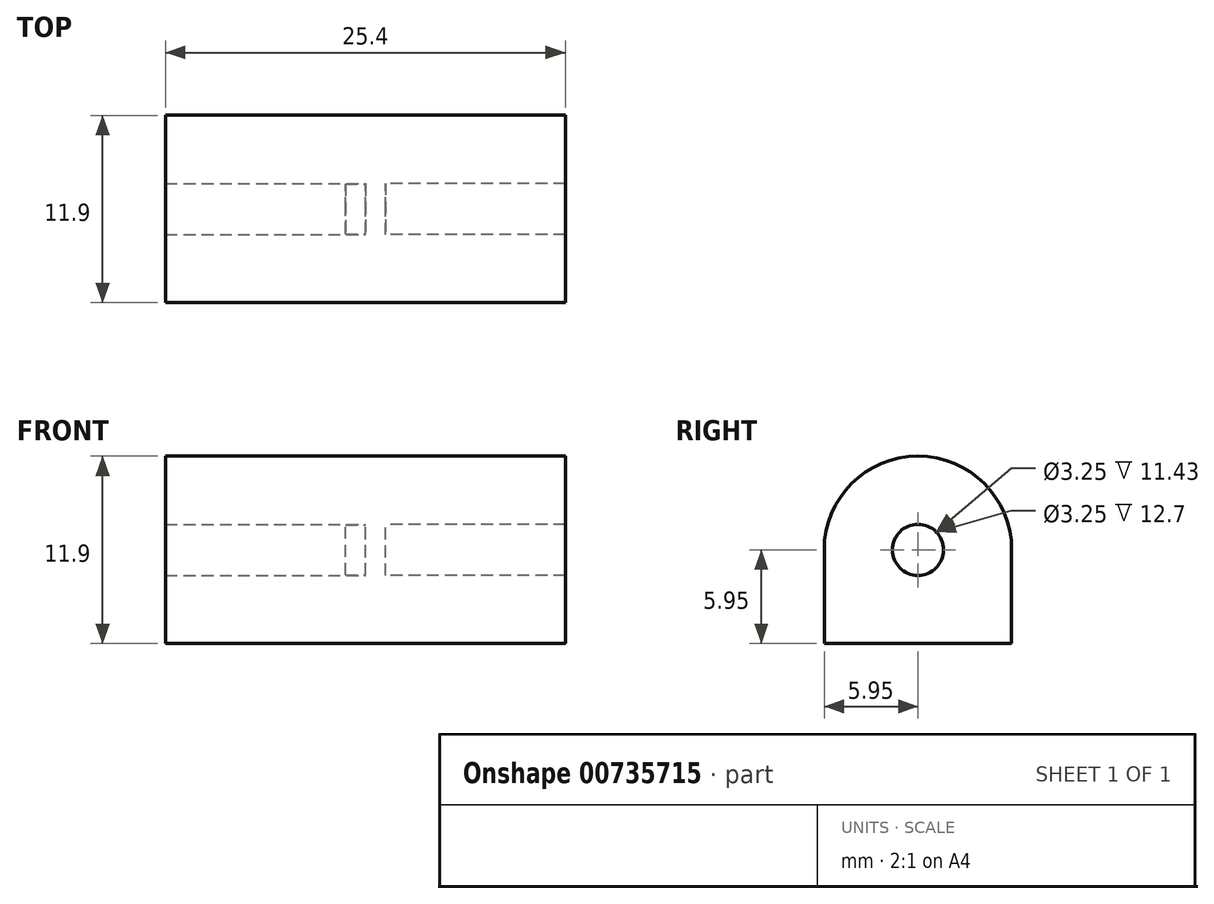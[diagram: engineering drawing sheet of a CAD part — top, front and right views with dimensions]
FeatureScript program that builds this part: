
annotation { "Feature Type Name" : "Feature", "Feature Type Description" : "" }
export const myFeature = defineFeature(function(context is Context, id is Id, definition is map)
    precondition{}
    {
        {
            var Q0;
            Q0=qCreatedBy(makeId("Right.planeOp"),FACE);
            var sketch = newSketch(context, id + "F0", { "sketchPlane" : qUnion([Q0])});
            skPoint(sketch, "E0", {"position": v(0, 0) * mm});
            skCircle(sketch, "E1", {"center": v(0, 0) * mm, "radius": 1.63 * mm});
            skCircle(sketch, "E2", {"center": v(0, 0) * mm, "radius": 5.95 * mm});
            skLineSegment(sketch, "E3", {"start": v(-5.95, 0) * mm, "end": v(-5.95, -5.95) * mm});
            skLineSegment(sketch, "E4", {"start": v(0, -5.95) * mm, "end": v(-5.95, -5.95) * mm});
            skLineSegment(sketch, "E5.MirrorCS", {"start": v(5.95, 0) * mm, "end": v(5.95, -5.95) * mm});
            skLineSegment(sketch, "E6.MirrorCS", {"start": v(0, -5.95) * mm, "end": v(5.95, -5.95) * mm});
            skSolve(sketch);
        }
        {
            var Q0;
            Q0=makeQuery(id+"F0.imprint","IMPRINT",FACE,{"disambiguationData":[TD([[makeQuery(id+"F0.imprint","IMPRINT",EDGE,{"derivedFrom":sQuery(id+"F0.wireOp",EDGE,"E1")}),-1.0]])]});
            var Q1;
            {var subQ0=sQuery(id+"F0.wireOp",EDGE,"LAxV7YV0-o3Pd-S6Uu-0Qhw-ZbayDCktP1mj");Q1=makeQuery(id+"F0.imprint","IMPRINT",FACE,{"disambiguationData":[TD([[makeQuery(id+"F0.imprint","IMPRINT",EDGE,{"derivedFrom":subQ0}),-1.0]])]});}
            var Q2;
            {var subQ0=sQuery(id+"F0.wireOp",EDGE,"a4slryUw-I1Qj-lKQd-dN9I-7wWvJhmVjrbc");Q2=makeQuery(id+"F0.imprint","IMPRINT",FACE,{"disambiguationData":[TD([[makeQuery(id+"F0.imprint","IMPRINT",EDGE,{"derivedFrom":subQ0}),-1.0]])]});}
            var Q3;
            {var subQ0=sQuery(id+"F0.wireOp",EDGE,"bc7faf61-ac77-4107-8db6-a5a29b3dcb3c0.MirrorCS");Q3=makeQuery(id+"F0.imprint","IMPRINT",FACE,{"disambiguationData":[TD([[makeQuery(id+"F0.imprint","IMPRINT",EDGE,{"derivedFrom":subQ0}),1.0]])]});}
            var Q4;
            {var subQ0=sQuery(id+"F0.wireOp",EDGE,"V9x5OHFx-vdUW-RZON-vu1w-wDtBgKBEigPh");Q4=makeQuery(id+"F0.imprint","IMPRINT",FACE,{"disambiguationData":[TD([[makeQuery(id+"F0.imprint","IMPRINT",EDGE,{"derivedFrom":subQ0}),-1.0]])]});}
            var Q5;
            {var subQ2=sQuery(id+"F0.wireOp",EDGE,"E5.MirrorCS");Q5=makeQuery(id+"F0.imprint","IMPRINT",FACE,{"disambiguationData":[TD([[makeQuery(id+"F0.imprint","IMPRINT",EDGE,{"derivedFrom":subQ2}),-1.0]])]});}
            var Q6;
            {var subQ0=sQuery(id+"F0.wireOp",EDGE,"E3");Q6=makeQuery(id+"F0.imprint","IMPRINT",FACE,{"disambiguationData":[TD([[makeQuery(id+"F0.imprint","IMPRINT",EDGE,{"derivedFrom":subQ0}),1.0]])]});}
            extrude(context, id + "F1", {"entities" : qUnion([Q0, Q1, Q2, Q3, Q4, Q5, Q6]), "depth" : 12.7 * mm, "offsetDistance" : 25.4 * mm});
        }
        {
            var Q0;
            Q0=qCreatedBy(makeId("Right.planeOp"),FACE);
            var sketch = newSketch(context, id + "F2", { "sketchPlane" : qUnion([Q0])});
            skCircle(sketch, "E7", {"center": v(0, 0) * mm, "radius": 1.59 * mm});
            skSolve(sketch);
        }
        {
            var Q0;
            Q0=makeQuery(id+"F0.imprint","IMPRINT",FACE,{"disambiguationData":[TD([[makeQuery(id+"F0.imprint","IMPRINT",EDGE,{"derivedFrom":sQuery(id+"F0.wireOp",EDGE,"E1")}),1.0]])]});
            extrude(context, id + "F3", {"entities" : qUnion([Q0]), "depth" : 1.27 * mm, "offsetDistance" : 25.4 * mm});
        }
        {
            var Q0;
            Q0=makeQuery(id+"F2.imprint","IMPRINT",FACE,{"disambiguationData":[TD([[makeQuery(id+"F2.imprint","IMPRINT",EDGE,{"derivedFrom":sQuery(id+"F2.wireOp",EDGE,"E7")}),1.0]])]});
            var Q1;
            Q1=sQuery(id+"F2.wireOp",EDGE,"E7");
            extrude(context, id + "F4", {"entities" : qUnion([Q0]), "surfaceEntities" : qUnion([Q1]), "depth" : -1.27 * mm, "offsetDistance" : 25.4 * mm});
        }
        {
            var Q0;
            Q0=makeQuery(id+"F0.imprint","IMPRINT",FACE,{"disambiguationData":[TD([[makeQuery(id+"F0.imprint","IMPRINT",EDGE,{"derivedFrom":sQuery(id+"F0.wireOp",EDGE,"E1")}),-1.0]])]});
            var Q1;
            {var subQ2=sQuery(id+"F0.wireOp",EDGE,"E5.MirrorCS");Q1=makeQuery(id+"F0.imprint","IMPRINT",FACE,{"disambiguationData":[TD([[makeQuery(id+"F0.imprint","IMPRINT",EDGE,{"derivedFrom":subQ2}),-1.0]])]});}
            var Q2;
            {var subQ0=sQuery(id+"F0.wireOp",EDGE,"E3");Q2=makeQuery(id+"F0.imprint","IMPRINT",FACE,{"disambiguationData":[TD([[makeQuery(id+"F0.imprint","IMPRINT",EDGE,{"derivedFrom":subQ0}),1.0]])]});}
            extrude(context, id + "F5", {"entities" : qUnion([Q0, Q1, Q2]), "operationType" : NewBodyOperationType.ADD, "depth" : -12.7 * mm, "offsetDistance" : 25.4 * mm});
        }
    });
